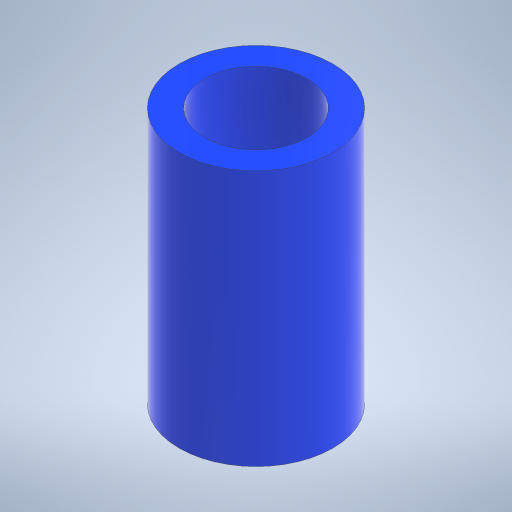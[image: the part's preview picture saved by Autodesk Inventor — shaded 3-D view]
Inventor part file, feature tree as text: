
AUTODESK INVENTOR PART (.ipt)
format: ipt  version: 2024.3 (Build 283343000, 343)  size: 213,504 bytes
history: native  units: mm
features: extrude x1, sketch x1
ambient origin geometry x8: Origin, YZ Plane, XZ Plane, XY Plane, X Axis, Y Axis, Z Axis, Center Point
bodies: Solid1 (feature_tree)
feature tree (2):
  extrude  "Extrusion1"  Depth=5.0mm
  sketch  "Sketch1"  dims[d0=3.0mm d1=2.0mm d2=5.0mm d3=0.0mm]
